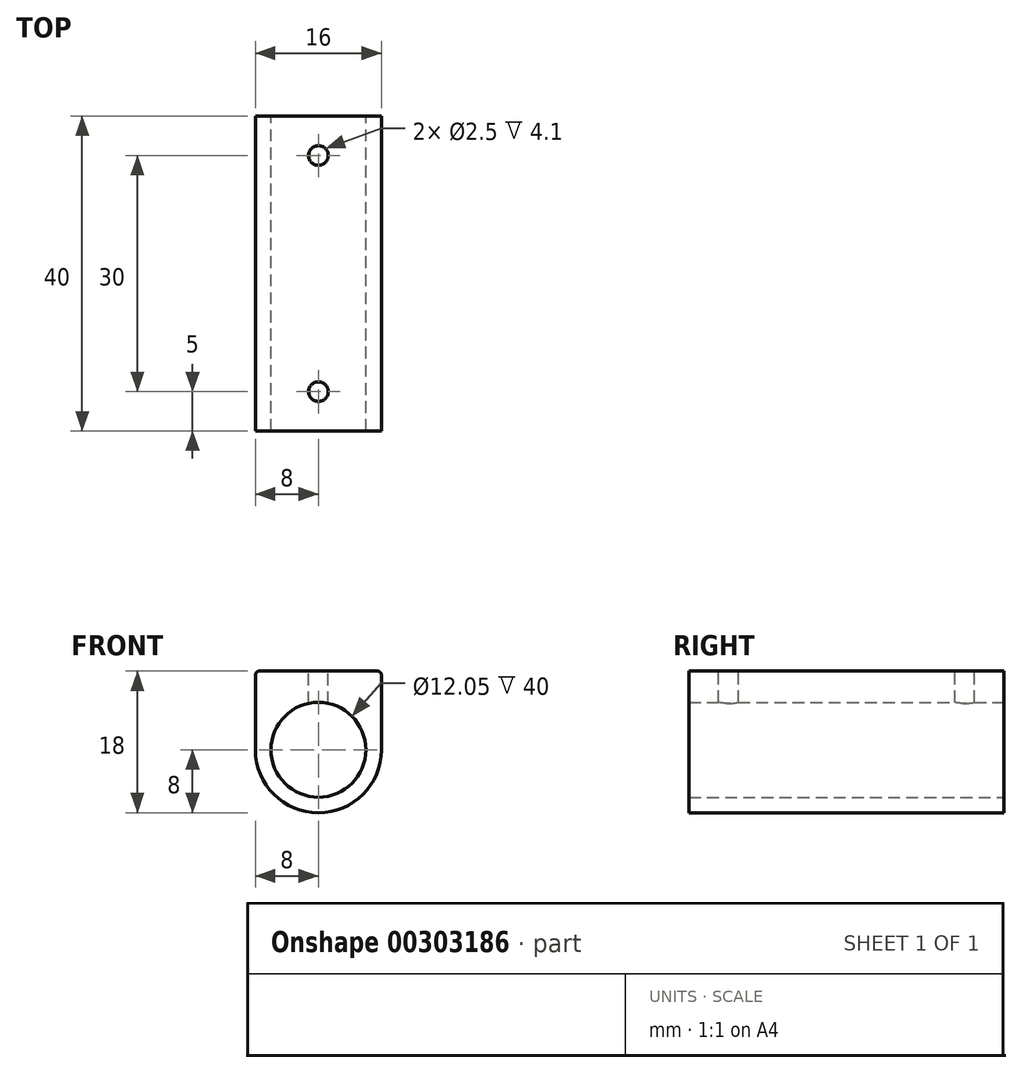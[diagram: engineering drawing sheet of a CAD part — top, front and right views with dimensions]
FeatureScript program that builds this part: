
annotation { "Feature Type Name" : "Feature", "Feature Type Description" : "" }
export const myFeature = defineFeature(function(context is Context, id is Id, definition is map)
    precondition{}
    {
        {
            var Q0;
            Q0=qCreatedBy(makeId("Front.planeOp"),FACE);
            var sketch = newSketch(context, id + "F0", { "sketchPlane" : qUnion([Q0])});
            skCircle(sketch, "E0", {"center": v(0, 0) * mm, "radius": 6.03 * mm});
            skArc(sketch, "E1", {"start": v(-8, 0) * mm, "mid": v(0, -8) * mm, "end": v(8, 0) * mm});
            skLineSegment(sketch, "E2", {"start": v(-8, 0) * mm, "end": v(-8, 10) * mm});
            skLineSegment(sketch, "E3", {"start": v(8, 0) * mm, "end": v(8, 10) * mm});
            skLineSegment(sketch, "E4", {"start": v(-8, 10) * mm, "end": v(8, 10) * mm});
            skSolve(sketch);
        }
        {
            var Q0;
            Q0 = qSketchRegion(id + "F0", true);
            extrude(context, id + "F1", {"entities" : qUnion([Q0]), "depth" : 40 * mm});
        }
        {
            var Q0;
            Q0=makeQuery(id+"F1.opExtrude","SWEPT_FACE",FACE,{"disambiguationData":[OSD([sQuery(id+"F0.wireOp",EDGE,"E4")])]});
            var sketch = newSketch(context, id + "F2", { "sketchPlane" : qUnion([Q0])});
            skCircle(sketch, "E5", {"center": v(0, -5) * mm, "radius": 1.25 * mm});
            skCircle(sketch, "E6", {"center": v(0, -35) * mm, "radius": 1.25 * mm});
            skSolve(sketch);
        }
        {
            var Q0;
            Q0 = qSketchRegion(id + "F2", true);
            extrude(context, id + "F3", {"entities" : qUnion([Q0]), "operationType" : NewBodyOperationType.REMOVE, "oppositeDirection" : true, "depth" : 4.1 * mm});
        }
        {
            var Q0;
            Q0=makeQuery(id+"F1.opExtrude","SWEPT_EDGE",EDGE,{"disambiguationData":[OSD([sQuery(id+"F0.wireOp",EDGE,"E2"),sQuery(id+"F0.wireOp",EDGE,"E4")])]});
            var Q1;
            Q1=makeQuery(id+"F1.opExtrude","SWEPT_EDGE",EDGE,{"disambiguationData":[OSD([sQuery(id+"F0.wireOp",EDGE,"E3"),sQuery(id+"F0.wireOp",EDGE,"E4")])]});
            fillet(context, id + "F4", {"entities" : qUnion([Q0, Q1]), "radius" : 0.5 * mm, "tangentPropagation" : true, "allowEdgeOverflow" : false});
        }
    });
